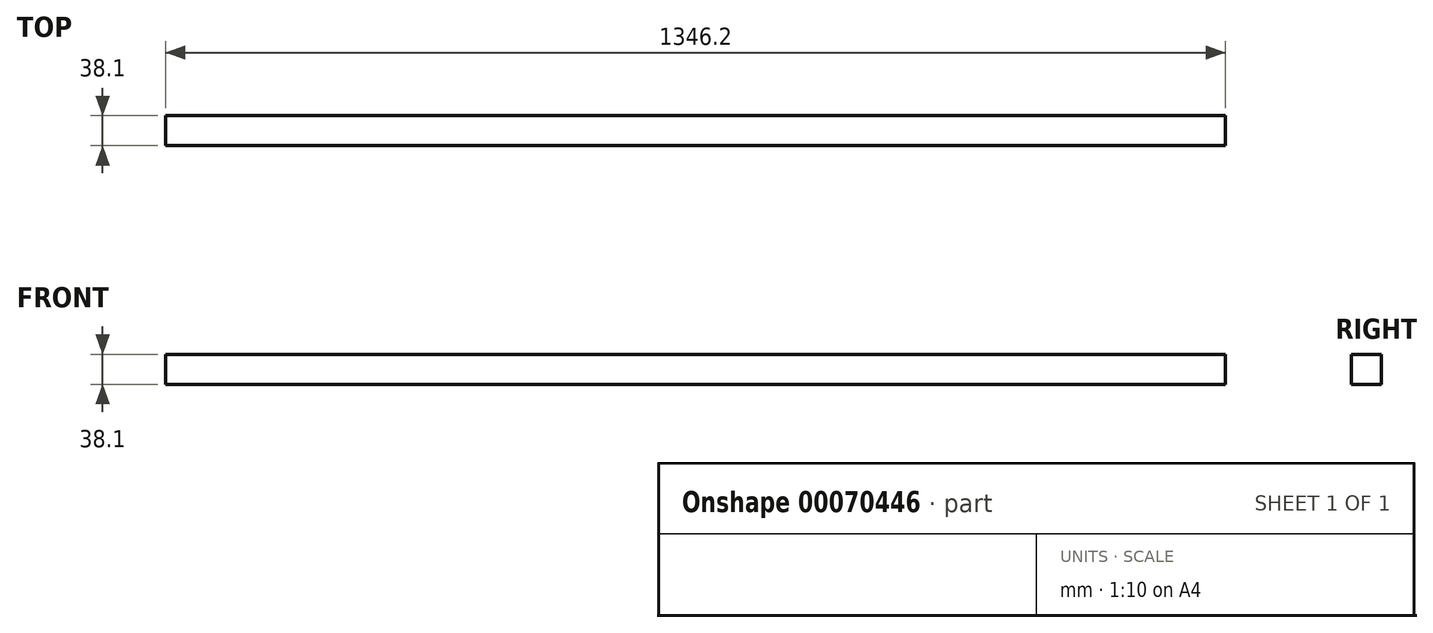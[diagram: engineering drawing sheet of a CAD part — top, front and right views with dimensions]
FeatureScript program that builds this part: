
annotation { "Feature Type Name" : "Feature", "Feature Type Description" : "" }
export const myFeature = defineFeature(function(context is Context, id is Id, definition is map)
    precondition{}
    {
        {
            var Q0;
            Q0=qCreatedBy(makeId("Right.planeOp"),FACE);
            var sketch = newSketch(context, id + "F0", { "sketchPlane" : qUnion([Q0])});
            skLineSegment(sketch, "E0.bottom", {"start": v(-26.11, 44.54) * mm, "end": v(11.99, 44.54) * mm});
            skLineSegment(sketch, "E0.top", {"start": v(-26.11, 6.44) * mm, "end": v(11.99, 6.44) * mm});
            skLineSegment(sketch, "E0.left", {"start": v(-26.11, 44.54) * mm, "end": v(-26.11, 6.44) * mm});
            skLineSegment(sketch, "E0.right", {"start": v(11.99, 44.54) * mm, "end": v(11.99, 6.44) * mm});
            skSolve(sketch);
        }
        {
            var Q0;
            Q0 = qSketchRegion(id + "F0", true);
            extrude(context, id + "F1", {"entities" : qUnion([Q0]), "oppositeDirection" : true, "depth" : 1346.2 * mm});
        }
    });
